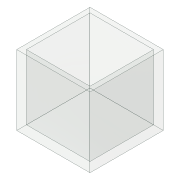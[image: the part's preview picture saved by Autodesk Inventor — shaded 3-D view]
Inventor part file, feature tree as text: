
AUTODESK INVENTOR PART (.ipt)
format: ipt  version: 2019 (Build 230136000, 136)  size: 90,624 bytes
history: native  units: mm
features: extrude x2, sketch x2
ambient origin geometry x8: Origin, YZ Plane, XZ Plane, XY Plane, X Axis, Y Axis, Z Axis, Center Point
bodies: Solid1 (feature_tree)
feature tree (4):
  extrude  "Extrusion1"  Depth=39.0mm
  extrude  "Extrusion2"  Depth=3.0mm
  sketch  "Sketch1"  dims[d0=39.0mm d1=39.0mm]
  sketch  "Sketch2"  dims[d2=3.0mm d3=3.0mm d4=3.0mm d5=3.0mm d6=40.0mm d7=0.0mm d8=3.0mm d9=0.0mm]
